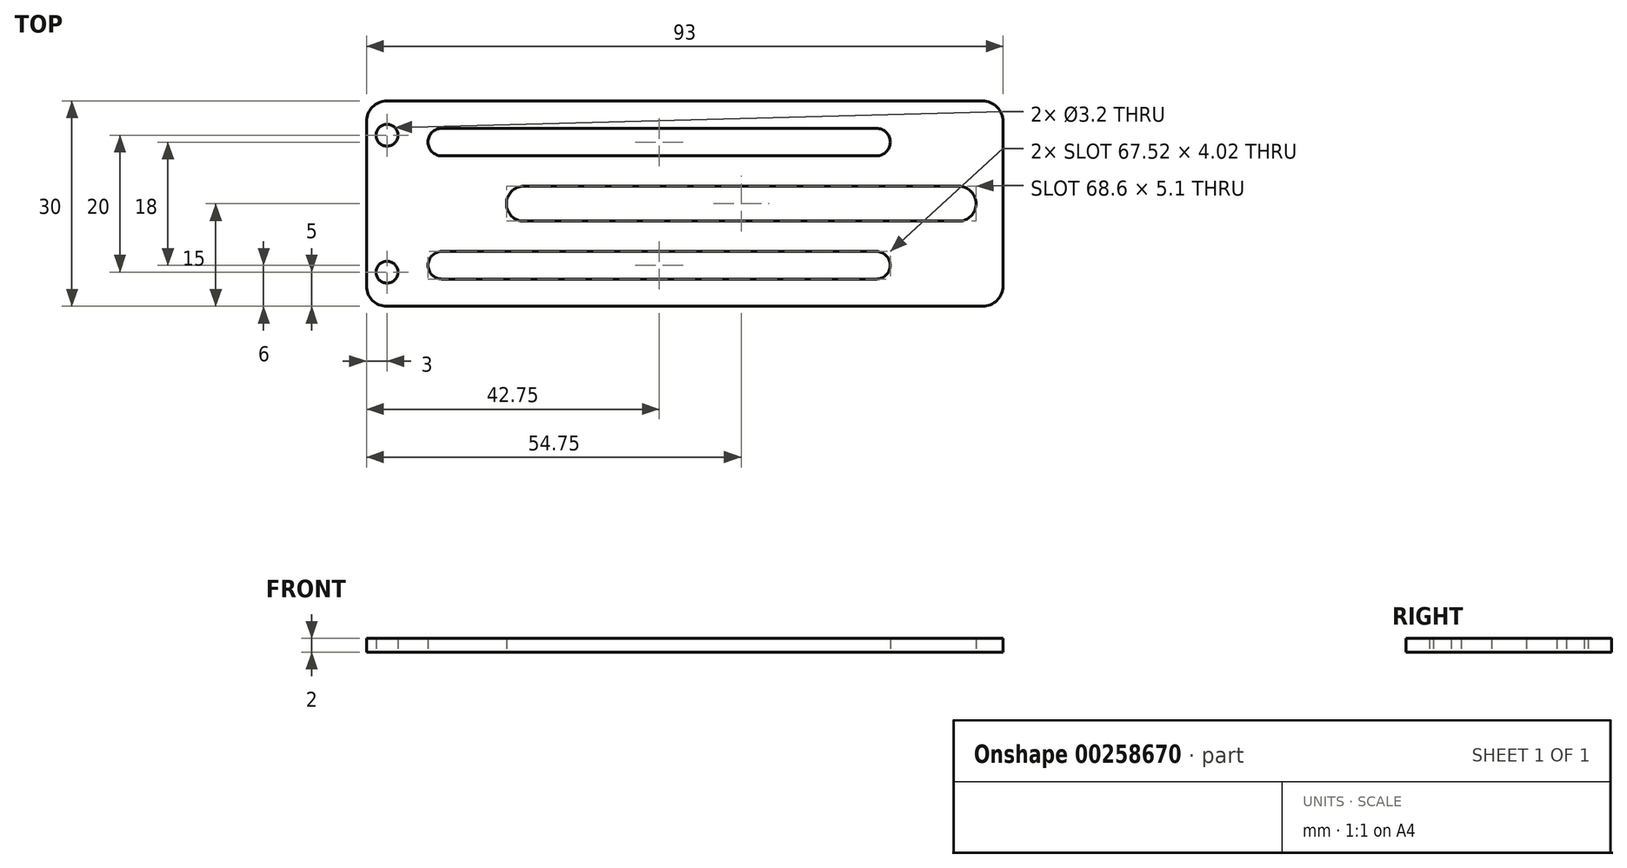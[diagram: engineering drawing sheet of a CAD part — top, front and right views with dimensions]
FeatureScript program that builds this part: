
annotation { "Feature Type Name" : "Feature", "Feature Type Description" : "" }
export const myFeature = defineFeature(function(context is Context, id is Id, definition is map)
    precondition{}
    {
        {
            var Q0;
            Q0=qCreatedBy(makeId("Top.planeOp"),FACE);
            var sketch = newSketch(context, id + "F0", { "sketchPlane" : qUnion([Q0])});
            skLineSegment(sketch, "E0.bottom", {"start": v(46.5, -15) * mm, "end": v(-46.5, -15) * mm});
            skLineSegment(sketch, "E0.top", {"start": v(46.5, 15) * mm, "end": v(-46.5, 15) * mm});
            skLineSegment(sketch, "E0.left", {"start": v(46.5, -15) * mm, "end": v(46.5, 15) * mm});
            skLineSegment(sketch, "E0.right", {"start": v(-46.5, -15) * mm, "end": v(-46.5, 15) * mm});
            skPoint(sketch, "E0.middle", {"position": v(0, 0) * mm});
            skLineSegment(sketch, "E1", {"start": v(0, 0) * mm, "end": v(8.25, 0) * mm});
            skLineSegment(sketch, "E2.bottom", {"start": v(40, -2.55) * mm, "end": v(-23.5, -2.55) * mm});
            skLineSegment(sketch, "E2.top", {"start": v(40, 2.55) * mm, "end": v(-23.5, 2.55) * mm});
            skLineSegment(sketch, "E2.left", {"start": v(40, -2.55) * mm, "end": v(40, 2.55) * mm});
            skLineSegment(sketch, "E2.right", {"start": v(-23.5, -2.55) * mm, "end": v(-23.5, 2.55) * mm});
            skPoint(sketch, "E2.middle", {"position": v(8.25, 0) * mm});
            skLineSegment(sketch, "E3", {"start": v(0, 0) * mm, "end": v(0, 9) * mm});
            skLineSegment(sketch, "E4", {"start": v(0, 9) * mm, "end": v(-3.75, 9) * mm});
            skLineSegment(sketch, "E5", {"start": v(0, 0) * mm, "end": v(0, -9) * mm});
            skLineSegment(sketch, "E6", {"start": v(0, -9) * mm, "end": v(-3.75, -9) * mm});
            skLineSegment(sketch, "E7.bottom", {"start": v(28, 7) * mm, "end": v(-35.5, 7) * mm});
            skLineSegment(sketch, "E7.top", {"start": v(28, 11.01) * mm, "end": v(-35.5, 11.01) * mm});
            skLineSegment(sketch, "E7.left", {"start": v(28, 7) * mm, "end": v(28, 11.01) * mm});
            skLineSegment(sketch, "E7.right", {"start": v(-35.5, 7) * mm, "end": v(-35.5, 11.01) * mm});
            skPoint(sketch, "E7.middle", {"position": v(-3.75, 9) * mm});
            skLineSegment(sketch, "E8.bottom", {"start": v(28, -11) * mm, "end": v(-35.5, -11) * mm});
            skLineSegment(sketch, "E8.top", {"start": v(28, -6.99) * mm, "end": v(-35.5, -6.99) * mm});
            skLineSegment(sketch, "E8.left", {"start": v(28, -11) * mm, "end": v(28, -6.99) * mm});
            skLineSegment(sketch, "E8.right", {"start": v(-35.5, -11) * mm, "end": v(-35.5, -6.99) * mm});
            skPoint(sketch, "E8.middle", {"position": v(-3.75, -9) * mm});
            skArc(sketch, "E9", {"start": v(40, -2.55) * mm, "mid": v(42.55, 0) * mm, "end": v(40, 2.55) * mm});
            skArc(sketch, "E10", {"start": v(-23.5, 2.55) * mm, "mid": v(-26.05, 0) * mm, "end": v(-23.5, -2.55) * mm});
            skArc(sketch, "E11", {"start": v(-35.5, -6.99) * mm, "mid": v(-37.51, -9) * mm, "end": v(-35.5, -11) * mm});
            skArc(sketch, "E12", {"start": v(28, -11) * mm, "mid": v(30.01, -9) * mm, "end": v(28, -6.99) * mm});
            skArc(sketch, "E13", {"start": v(-35.5, 11.01) * mm, "mid": v(-37.51, 9) * mm, "end": v(-35.5, 7) * mm});
            skArc(sketch, "E14", {"start": v(28, 7) * mm, "mid": v(30.01, 9) * mm, "end": v(28, 11.01) * mm});
            skLineSegment(sketch, "E15", {"start": v(0, 0) * mm, "end": v(-46.5, 0) * mm});
            skLineSegment(sketch, "E16", {"start": v(-46.5, 0) * mm, "end": v(-46.5, 10) * mm});
            skLineSegment(sketch, "E17", {"start": v(-46.5, 10) * mm, "end": v(-43.5, 10) * mm});
            skLineSegment(sketch, "E18", {"start": v(-43.5, 10) * mm, "end": v(-43.5, -10) * mm});
            skCircle(sketch, "E19", {"center": v(-43.5, 10) * mm, "radius": 1.6 * mm});
            skCircle(sketch, "E20", {"center": v(-43.5, -10) * mm, "radius": 1.6 * mm});
            skSolve(sketch);
        }
        {
            var Q0;
            Q0 = qSketchRegion(id + "F0", true);
            extrude(context, id + "F1", {"entities" : qUnion([Q0]), "depth" : 2 * mm});
        }
        {
            var Q0;
            Q0=makeQuery(id+"F1.opExtrude","SWEPT_EDGE",EDGE,{"disambiguationData":[OSD([sQuery(id+"F0.wireOp",EDGE,"E0.bottom"),sQuery(id+"F0.wireOp",EDGE,"E0.right")])]});
            var Q1;
            Q1=makeQuery(id+"F1.opExtrude","SWEPT_EDGE",EDGE,{"disambiguationData":[OSD([sQuery(id+"F0.wireOp",EDGE,"E0.bottom"),sQuery(id+"F0.wireOp",EDGE,"E0.left")])]});
            var Q2;
            Q2=makeQuery(id+"F1.opExtrude","SWEPT_EDGE",EDGE,{"disambiguationData":[OSD([sQuery(id+"F0.wireOp",EDGE,"E0.top"),sQuery(id+"F0.wireOp",EDGE,"E0.left")])]});
            var Q3;
            Q3=makeQuery(id+"F1.opExtrude","SWEPT_EDGE",EDGE,{"disambiguationData":[OSD([sQuery(id+"F0.wireOp",EDGE,"E0.top"),sQuery(id+"F0.wireOp",EDGE,"E0.right")])]});
            fillet(context, id + "F2", {"entities" : qUnion([Q0, Q1, Q2, Q3]), "radius" : 3 * mm, "tangentPropagation" : true, "allowEdgeOverflow" : false});
        }
    });
